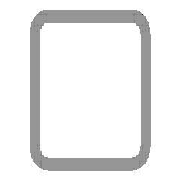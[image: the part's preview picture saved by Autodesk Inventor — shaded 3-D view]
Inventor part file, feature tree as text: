
AUTODESK INVENTOR PART (.ipt)
format: ipt  version: 2025 (Build 290162010, 162A)  size: 150,016 bytes
history: native  units: mm (DEFAULTED — no unit token found)
features: other x4, plane x3, split x2, sketch x1
ambient origin geometry x8: Origin, YZ Plane, XZ Plane, XY Plane, X Axis, Y Axis, Z Axis, Center Point
bodies: Solid1 (feature_tree), Body (feature_tree)
feature tree (10):
  parser-record x1  (decoder bookkeeping rows leaked as tree rows — omitted from the tree; the rows remain in map.json)
  other  "Driven Length"
  other  "Start Plane"
  other  "End Plane"
  plane  "Work Plane4"
  split  "Split1"
  plane  "Work Plane5"
  split  "Split2"
  sketch  "Sketch3"  dims[d3=2064.751801mm d4=0.0mm d7=4.0mm d9=40.0mm d11=40.0mm d12=2.0mm d13=-0.0mm d14=2064.751801mm d15=20.0mm d16=20.0mm d17=90.0deg d18=2064.751801mm]
  plane  "Work Plane3"
